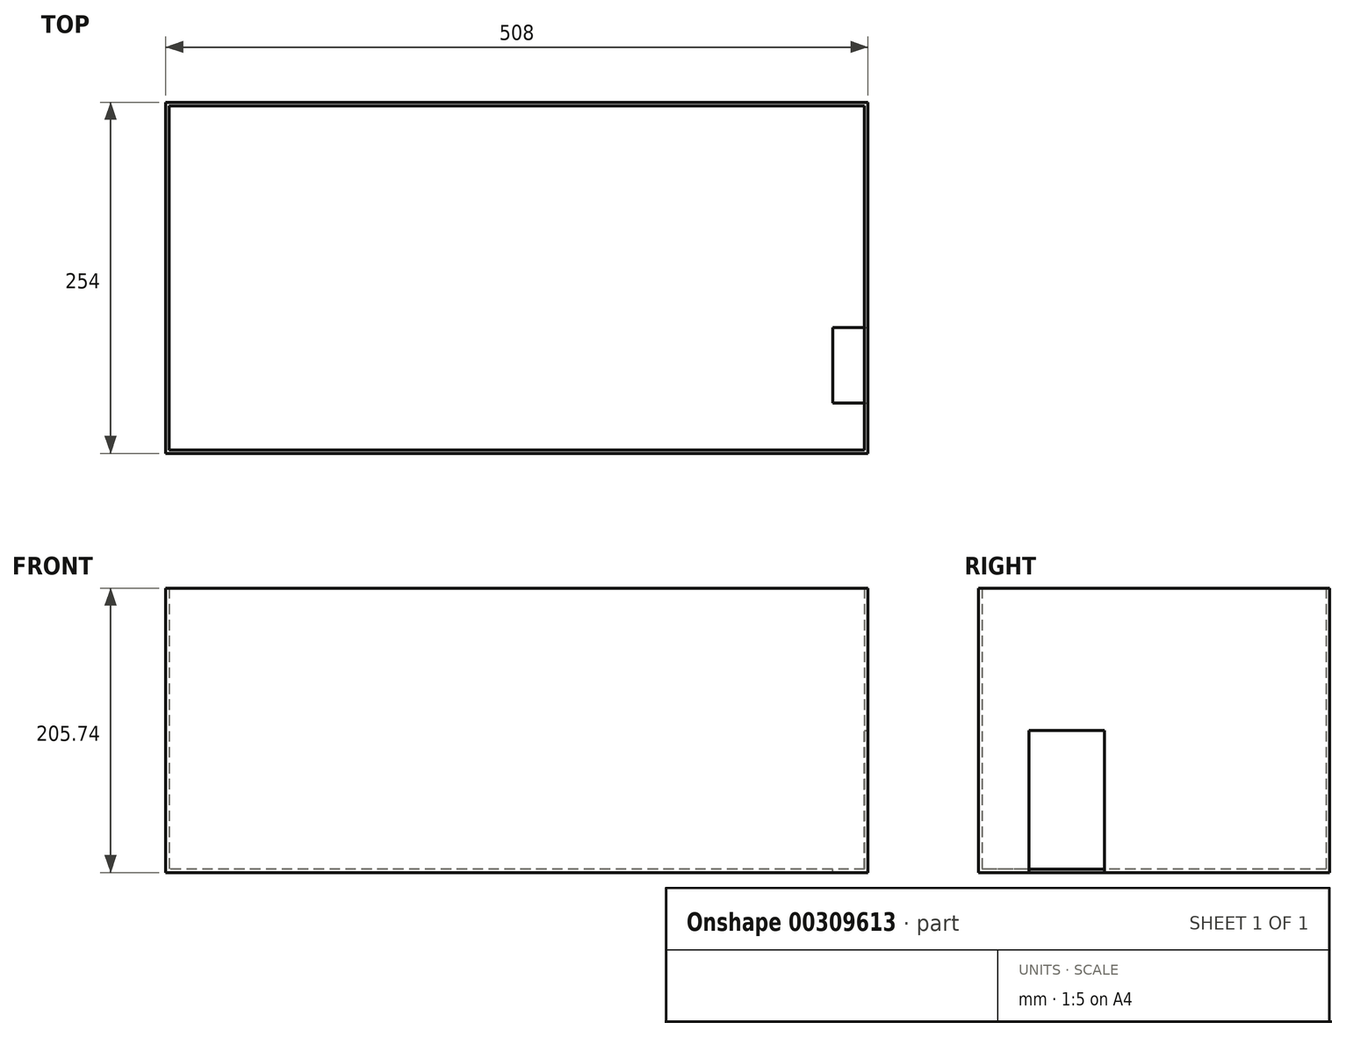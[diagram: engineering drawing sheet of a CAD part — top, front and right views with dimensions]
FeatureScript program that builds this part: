
annotation { "Feature Type Name" : "Feature", "Feature Type Description" : "" }
export const myFeature = defineFeature(function(context is Context, id is Id, definition is map)
    precondition{}
    {
        {
            var Q0;
            Q0=qCreatedBy(makeId("Top.planeOp"),FACE);
            var sketch = newSketch(context, id + "F0", { "sketchPlane" : qUnion([Q0])});
            skLineSegment(sketch, "E0.bottom", {"start": v(254, -127) * mm, "end": v(-254, -127) * mm});
            skLineSegment(sketch, "E0.top", {"start": v(254, 127) * mm, "end": v(-254, 127) * mm});
            skLineSegment(sketch, "E0.left", {"start": v(254, -127) * mm, "end": v(254, 127) * mm});
            skLineSegment(sketch, "E0.right", {"start": v(-254, -127) * mm, "end": v(-254, 127) * mm});
            skPoint(sketch, "E0.middle", {"position": v(0, 0) * mm});
            skSolve(sketch);
        }
        {
            var Q0;
            Q0 = qSketchRegion(id + "F0", true);
            extrude(context, id + "F1", {"entities" : qUnion([Q0]), "depth" : 2.54 * mm});
        }
        {
            var Q0;
            Q0=makeQuery(id+"F1.opExtrude","CAP_FACE",FACE,{"disambiguationData":[OSD([sQuery(id+"F0.wireOp",EDGE,"E0.bottom"),sQuery(id+"F0.wireOp",EDGE,"E0.top"),sQuery(id+"F0.wireOp",EDGE,"E0.left"),sQuery(id+"F0.wireOp",EDGE,"E0.right")])],"isStart":false});
            var sketch = newSketch(context, id + "F2", { "sketchPlane" : qUnion([Q0])});
            skLineSegment(sketch, "E1.bottom", {"start": v(-254, 127) * mm, "end": v(-251.46, 127) * mm});
            skLineSegment(sketch, "E1.top", {"start": v(-254, -127) * mm, "end": v(-251.46, -127) * mm});
            skLineSegment(sketch, "E1.left", {"start": v(-254, 127) * mm, "end": v(-254, -127) * mm});
            skLineSegment(sketch, "E1.right", {"start": v(-251.46, 127) * mm, "end": v(-251.46, -127) * mm});
            skLineSegment(sketch, "E2.bottom", {"start": v(254, 127) * mm, "end": v(-251.46, 127) * mm});
            skLineSegment(sketch, "E2.top", {"start": v(254, 124.46) * mm, "end": v(-251.46, 124.46) * mm});
            skLineSegment(sketch, "E2.left", {"start": v(254, 127) * mm, "end": v(254, 124.46) * mm});
            skLineSegment(sketch, "E2.right", {"start": v(-251.46, 127) * mm, "end": v(-251.46, 124.46) * mm});
            skSolve(sketch);
        }
        {
            var Q0;
            Q0 = qSketchRegion(id + "F2", true);
            extrude(context, id + "F3", {"entities" : qUnion([Q0]), "operationType" : NewBodyOperationType.ADD, "depth" : 203.2 * mm});
        }
        {
            var Q0;
            Q0=makeQuery(id+"F1.opExtrude","CAP_FACE",FACE,{"disambiguationData":[OSD([sQuery(id+"F0.wireOp",EDGE,"E0.bottom"),sQuery(id+"F0.wireOp",EDGE,"E0.top"),sQuery(id+"F0.wireOp",EDGE,"E0.left"),sQuery(id+"F0.wireOp",EDGE,"E0.right")])],"isStart":false});
            var sketch = newSketch(context, id + "F4", { "sketchPlane" : qUnion([Q0])});
            skLineSegment(sketch, "E3.right", {"start": v(-251.46, -130.32) * mm, "end": v(-251.46, -124.46) * mm});
            skLineSegment(sketch, "E4.bottom", {"start": v(254, -127) * mm, "end": v(-251.46, -127) * mm});
            skLineSegment(sketch, "E4.top", {"start": v(254, -124.46) * mm, "end": v(-251.46, -124.46) * mm});
            skLineSegment(sketch, "E4.left", {"start": v(254, -127) * mm, "end": v(254, -124.46) * mm});
            skLineSegment(sketch, "E4.right", {"start": v(-251.46, -127) * mm, "end": v(-251.46, -124.46) * mm});
            skLineSegment(sketch, "E5.bottom", {"start": v(254, 124.46) * mm, "end": v(251.46, 124.46) * mm});
            skLineSegment(sketch, "E5.top", {"start": v(254, -124.46) * mm, "end": v(251.46, -124.46) * mm});
            skLineSegment(sketch, "E5.left", {"start": v(254, 124.46) * mm, "end": v(254, -124.46) * mm});
            skLineSegment(sketch, "E5.right", {"start": v(251.46, 124.46) * mm, "end": v(251.46, -124.46) * mm});
            skSolve(sketch);
        }
        {
            var Q0;
            Q0 = qSketchRegion(id + "F4", true);
            extrude(context, id + "F5", {"entities" : qUnion([Q0]), "operationType" : NewBodyOperationType.ADD, "depth" : 203.2 * mm});
        }
        {
            var Q0;
            Q0=makeQuery(id+"F5.boolean.opBoolean","MERGE",FACE,{"derivedFrom":[makeQuery(id+"F3.boolean.opBoolean","MERGE",FACE,{"derivedFrom":[makeQuery(id+"F1.opExtrude","SWEPT_FACE",FACE,{"disambiguationData":[OSD([sQuery(id+"F0.wireOp",EDGE,"E0.left")])]}),makeQuery(id+"F3.opExtrude","SWEPT_FACE",FACE,{"disambiguationData":[OSD([sQuery(id+"F2.wireOp",EDGE,"E2.left")])]})]}),makeQuery(id+"F5.opExtrude","SWEPT_FACE",FACE,{"disambiguationData":[OSD([sQuery(id+"F4.wireOp",EDGE,"E4.left"),sQuery(id+"F4.wireOp",EDGE,"E5.left")])]})]});
            var sketch = newSketch(context, id + "F6", { "sketchPlane" : qUnion([Q0])});
            skPoint(sketch, "E6.oppositeSnap0", {"position": v(-127, 102.87) * mm});
            skLineSegment(sketch, "E6.bottom", {"start": v(-90.69, 0) * mm, "end": v(-35.96, 0) * mm});
            skLineSegment(sketch, "E6.top", {"start": v(-90.69, 102.87) * mm, "end": v(-35.96, 102.87) * mm});
            skLineSegment(sketch, "E6.left", {"start": v(-90.69, 0) * mm, "end": v(-90.69, 102.87) * mm});
            skLineSegment(sketch, "E6.right", {"start": v(-35.96, 0) * mm, "end": v(-35.96, 102.87) * mm});
            skSolve(sketch);
        }
        {
            var Q0;
            Q0 = qSketchRegion(id + "F6", true);
            extrude(context, id + "F7", {"entities" : qUnion([Q0]), "operationType" : NewBodyOperationType.REMOVE, "oppositeDirection" : true, "depth" : 25.4 * mm});
        }
    });
